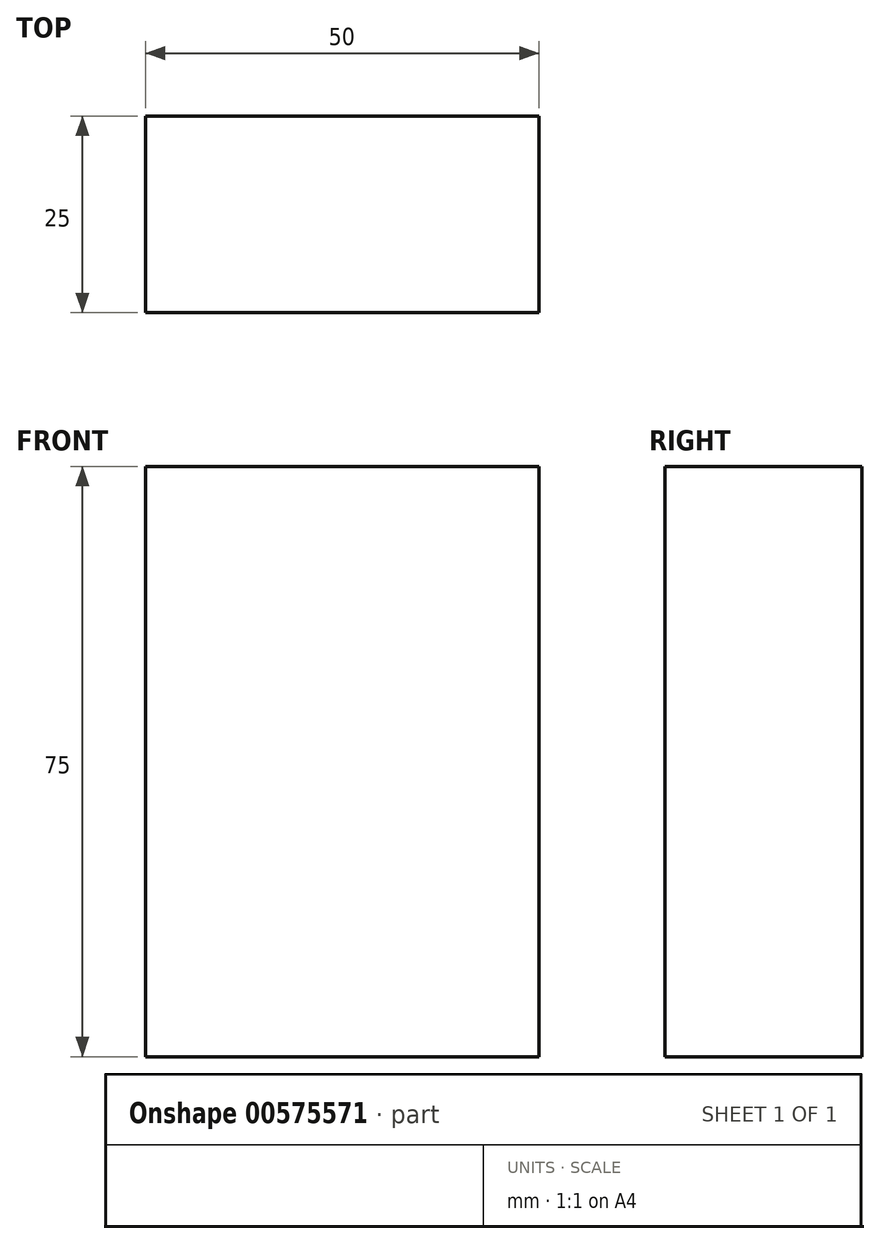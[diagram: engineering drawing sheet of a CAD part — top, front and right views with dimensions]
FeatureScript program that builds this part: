
annotation { "Feature Type Name" : "Feature", "Feature Type Description" : "" }
export const myFeature = defineFeature(function(context is Context, id is Id, definition is map)
    precondition{}
    {
        {
            var Q0;
            Q0=qCreatedBy(makeId("Top.planeOp"),FACE);
            var sketch = newSketch(context, id + "F0", { "sketchPlane" : qUnion([Q0])});
            skLineSegment(sketch, "E0.bottom", {"start": v(0, 0) * mm, "end": v(50, 0) * mm});
            skLineSegment(sketch, "E0.top", {"start": v(0, 25) * mm, "end": v(50, 25) * mm});
            skLineSegment(sketch, "E0.left", {"start": v(0, 0) * mm, "end": v(0, 25) * mm});
            skLineSegment(sketch, "E0.right", {"start": v(50, 0) * mm, "end": v(50, 25) * mm});
            skSolve(sketch);
        }
        {
            var Q0;
            Q0=makeQuery(id+"F0.imprint","IMPRINT",FACE,{"disambiguationData":[TD([[makeQuery(id+"F0.imprint","IMPRINT",EDGE,{"derivedFrom":sQuery(id+"F0.wireOp",EDGE,"E0.bottom")}),1.0]])]});
            extrude(context, id + "F1", {"entities" : qUnion([Q0]), "depth" : 75 * mm, "offsetDistance" : 25 * mm});
        }
    });
